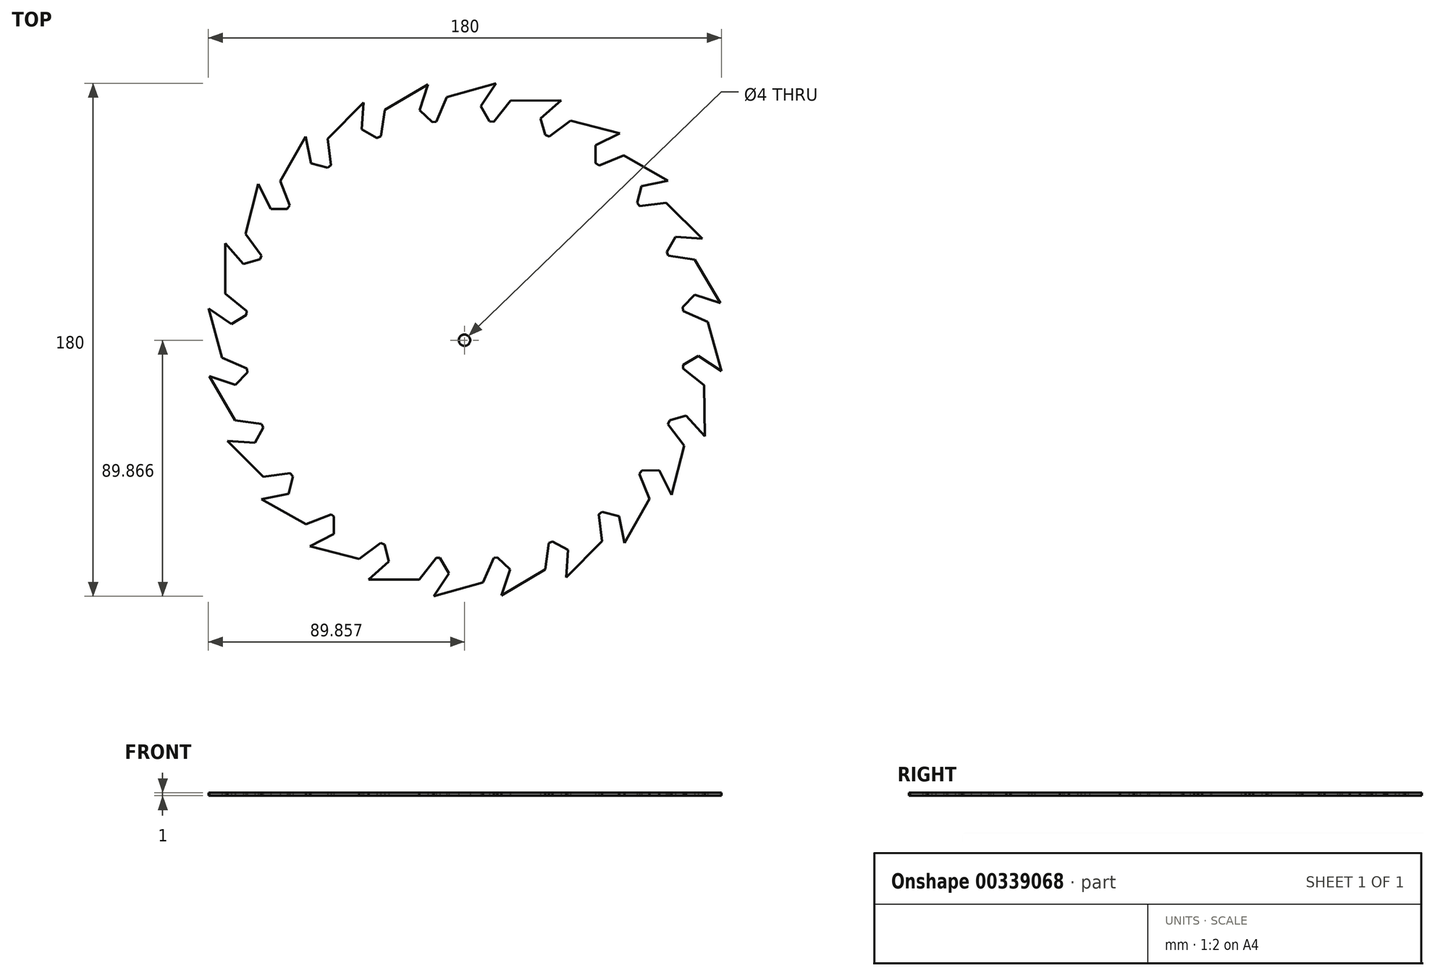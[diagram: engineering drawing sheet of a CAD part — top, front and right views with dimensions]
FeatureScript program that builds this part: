
annotation { "Feature Type Name" : "Feature", "Feature Type Description" : "" }
export const myFeature = defineFeature(function(context is Context, id is Id, definition is map)
    precondition{}
    {
        {
            var Q0;
            Q0=qCreatedBy(makeId("Top.planeOp"),FACE);
            var sketch = newSketch(context, id + "F0", { "sketchPlane" : qUnion([Q0])});
            skLineSegment(sketch, "E0", {"start": v(-178.94, 100.4) * mm, "end": v(-174.2, 83.11) * mm});
            skLineSegment(sketch, "E1", {"start": v(-174.2, 83.11) * mm, "end": v(-165.4, 79.33) * mm});
            skLineSegment(sketch, "E2", {"start": v(-165.4, 79.33) * mm, "end": v(-165.3, 77.88) * mm});
            skLineSegment(sketch, "E3", {"start": v(-165.3, 77.88) * mm, "end": v(-169.49, 73.59) * mm});
            skLineSegment(sketch, "E4", {"start": v(-169.49, 73.59) * mm, "end": v(-178.64, 76.7) * mm});
            skLineSegment(sketch, "E5", {"start": v(-178.64, 76.7) * mm, "end": v(-169.58, 61.17) * mm});
            skLineSegment(sketch, "E6", {"start": v(-169.58, 61.17) * mm, "end": v(-160.31, 59.89) * mm});
            skLineSegment(sketch, "E7", {"start": v(-160.31, 59.89) * mm, "end": v(-159.7, 58.58) * mm});
            skLineSegment(sketch, "E8", {"start": v(-159.7, 58.58) * mm, "end": v(-162.63, 53.3) * mm});
            skLineSegment(sketch, "E9", {"start": v(-162.63, 53.3) * mm, "end": v(-172.27, 53.87) * mm});
            skLineSegment(sketch, "E10", {"start": v(-172.27, 53.87) * mm, "end": v(-159.7, 41.3) * mm});
            skLineSegment(sketch, "E11", {"start": v(-159.7, 41.3) * mm, "end": v(-150.33, 42.55) * mm});
            skLineSegment(sketch, "E12", {"start": v(-150.33, 42.55) * mm, "end": v(-149.3, 41.4) * mm});
            skLineSegment(sketch, "E13", {"start": v(-149.3, 41.4) * mm, "end": v(-150.84, 35.4) * mm});
            skLineSegment(sketch, "E14", {"start": v(-150.84, 35.4) * mm, "end": v(-160.3, 33.5) * mm});
            skLineSegment(sketch, "E15", {"start": v(-160.3, 33.5) * mm, "end": v(-144.68, 24.66) * mm});
            skLineSegment(sketch, "E16", {"start": v(-144.68, 24.66) * mm, "end": v(-135.85, 28.17) * mm});
            skLineSegment(sketch, "E17", {"start": v(-135.85, 28.17) * mm, "end": v(-134.9, 27.37) * mm});
            skLineSegment(sketch, "E18", {"start": v(-134.9, 27.37) * mm, "end": v(-134.9, 21.23) * mm});
            skLineSegment(sketch, "E19", {"start": v(-134.9, 21.23) * mm, "end": v(-143.3, 16.95) * mm});
            skLineSegment(sketch, "E20", {"start": v(-143.3, 16.95) * mm, "end": v(-126.04, 12.48) * mm});
            skLineSegment(sketch, "E21", {"start": v(-126.04, 12.48) * mm, "end": v(-118.52, 18.08) * mm});
            skLineSegment(sketch, "E22", {"start": v(-118.52, 18.08) * mm, "end": v(-117.21, 17.6) * mm});
            skLineSegment(sketch, "E23", {"start": v(-117.21, 17.6) * mm, "end": v(-115.58, 11.63) * mm});
            skLineSegment(sketch, "E24", {"start": v(-115.58, 11.63) * mm, "end": v(-122.7, 5.3) * mm});
            skLineSegment(sketch, "E25", {"start": v(-122.7, 5.3) * mm, "end": v(-104.92, 5.3) * mm});
            skLineSegment(sketch, "E26", {"start": v(-104.92, 5.3) * mm, "end": v(-98.99, 12.84) * mm});
            skLineSegment(sketch, "E27", {"start": v(-98.99, 12.84) * mm, "end": v(-97.75, 12.84) * mm});
            skLineSegment(sketch, "E28", {"start": v(-97.75, 12.84) * mm, "end": v(-94.54, 7.4) * mm});
            skLineSegment(sketch, "E29", {"start": v(-94.54, 7.4) * mm, "end": v(-99.82, -0.6) * mm});
            skLineSegment(sketch, "E30", {"start": v(-99.82, -0.6) * mm, "end": v(-82.64, 4.2) * mm});
            skLineSegment(sketch, "E31", {"start": v(-82.64, 4.2) * mm, "end": v(-78.8, 12.84) * mm});
            skLineSegment(sketch, "E32", {"start": v(-78.8, 12.84) * mm, "end": v(-77.54, 13) * mm});
            skLineSegment(sketch, "E33", {"start": v(-77.54, 13) * mm, "end": v(-73.14, 8.78) * mm});
            skLineSegment(sketch, "E34", {"start": v(-73.14, 8.78) * mm, "end": v(-76.11, -0.27) * mm});
            skLineSegment(sketch, "E35", {"start": v(-76.11, -0.27) * mm, "end": v(-60.77, 8.78) * mm});
            skLineSegment(sketch, "E36", {"start": v(-60.77, 8.78) * mm, "end": v(-59.46, 18.1) * mm});
            skLineSegment(sketch, "E37", {"start": v(-59.46, 18.1) * mm, "end": v(-58.18, 18.66) * mm});
            skLineSegment(sketch, "E38", {"start": v(-58.18, 18.66) * mm, "end": v(-52.76, 15.66) * mm});
            skLineSegment(sketch, "E39", {"start": v(-52.76, 15.66) * mm, "end": v(-53.42, 6.03) * mm});
            skLineSegment(sketch, "E40", {"start": v(-53.42, 6.03) * mm, "end": v(-40.86, 18.77) * mm});
            skLineSegment(sketch, "E41", {"start": v(-40.86, 18.77) * mm, "end": v(-41.97, 28.14) * mm});
            skLineSegment(sketch, "E42", {"start": v(-41.97, 28.14) * mm, "end": v(-40.86, 29.07) * mm});
            skLineSegment(sketch, "E43", {"start": v(-40.86, 29.07) * mm, "end": v(-34.91, 27.53) * mm});
            skLineSegment(sketch, "E44", {"start": v(-34.91, 27.53) * mm, "end": v(-33, 18.1) * mm});
            skLineSegment(sketch, "E45", {"start": v(-33, 18.1) * mm, "end": v(-24.2, 33.57) * mm});
            skLineSegment(sketch, "E46", {"start": v(-24.2, 33.57) * mm, "end": v(-27.71, 42.4) * mm});
            skLineSegment(sketch, "E47", {"start": v(-27.71, 42.4) * mm, "end": v(-26.9, 43.5) * mm});
            skLineSegment(sketch, "E48", {"start": v(-26.9, 43.5) * mm, "end": v(-20.78, 43.6) * mm});
            skLineSegment(sketch, "E49", {"start": v(-20.78, 43.6) * mm, "end": v(-16.44, 35.03) * mm});
            skLineSegment(sketch, "E50", {"start": v(-16.44, 35.03) * mm, "end": v(-12, 52.31) * mm});
            skLineSegment(sketch, "E51", {"start": v(-12, 52.31) * mm, "end": v(-17.67, 59.77) * mm});
            skLineSegment(sketch, "E52", {"start": v(-17.67, 59.77) * mm, "end": v(-17.1, 61.17) * mm});
            skLineSegment(sketch, "E53", {"start": v(-17.1, 61.17) * mm, "end": v(-11.31, 62.78) * mm});
            skLineSegment(sketch, "E54", {"start": v(-11.31, 62.78) * mm, "end": v(-4.8, 55.6) * mm});
            skLineSegment(sketch, "E55", {"start": v(-4.8, 55.6) * mm, "end": v(-4.97, 73.5) * mm});
            skLineSegment(sketch, "E56", {"start": v(-4.97, 73.5) * mm, "end": v(-12.4, 79.3) * mm});
            skLineSegment(sketch, "E57", {"start": v(-12.4, 79.3) * mm, "end": v(-12.32, 80.62) * mm});
            skLineSegment(sketch, "E58", {"start": v(-12.32, 80.62) * mm, "end": v(-7, 83.76) * mm});
            skLineSegment(sketch, "E59", {"start": v(-7, 83.76) * mm, "end": v(1.06, 78.47) * mm});
            skLineSegment(sketch, "E60", {"start": v(1.06, 78.47) * mm, "end": v(-3.74, 95.75) * mm});
            skLineSegment(sketch, "E61", {"start": v(-3.74, 95.75) * mm, "end": v(-12.32, 99.47) * mm});
            skLineSegment(sketch, "E62", {"start": v(-12.32, 99.47) * mm, "end": v(-12.47, 100.94) * mm});
            skLineSegment(sketch, "E63", {"start": v(-12.47, 100.94) * mm, "end": v(-8.35, 105.22) * mm});
            skLineSegment(sketch, "E64", {"start": v(-8.35, 105.22) * mm, "end": v(0.74, 102.23) * mm});
            skLineSegment(sketch, "E65", {"start": v(0.74, 102.23) * mm, "end": v(-8.27, 117.52) * mm});
            skLineSegment(sketch, "E66", {"start": v(-8.27, 117.52) * mm, "end": v(-17.52, 118.92) * mm});
            skLineSegment(sketch, "E67", {"start": v(-17.52, 118.92) * mm, "end": v(-18.1, 120.24) * mm});
            skLineSegment(sketch, "E68", {"start": v(-18.1, 120.24) * mm, "end": v(-15.07, 125.58) * mm});
            skLineSegment(sketch, "E69", {"start": v(-15.07, 125.58) * mm, "end": v(-5.6, 124.93) * mm});
            skLineSegment(sketch, "E70", {"start": v(-5.6, 124.93) * mm, "end": v(-18.3, 137.44) * mm});
            skLineSegment(sketch, "E71", {"start": v(-18.3, 137.44) * mm, "end": v(-27.66, 136.3) * mm});
            skLineSegment(sketch, "E72", {"start": v(-27.66, 136.3) * mm, "end": v(-28.56, 137.44) * mm});
            skLineSegment(sketch, "E73", {"start": v(-28.56, 137.44) * mm, "end": v(-27.03, 143.36) * mm});
            skLineSegment(sketch, "E74", {"start": v(-27.03, 143.36) * mm, "end": v(-17.68, 145.27) * mm});
            skLineSegment(sketch, "E75", {"start": v(-17.68, 145.27) * mm, "end": v(-33.18, 154.08) * mm});
            skLineSegment(sketch, "E76", {"start": v(-33.18, 154.08) * mm, "end": v(-41.85, 150.55) * mm});
            skLineSegment(sketch, "E77", {"start": v(-41.85, 150.55) * mm, "end": v(-43.13, 151.46) * mm});
            skLineSegment(sketch, "E78", {"start": v(-43.13, 151.46) * mm, "end": v(-43.13, 157.6) * mm});
            skLineSegment(sketch, "E79", {"start": v(-43.13, 157.6) * mm, "end": v(-34.62, 161.85) * mm});
            skLineSegment(sketch, "E80", {"start": v(-34.62, 161.85) * mm, "end": v(-51.87, 166.3) * mm});
            skLineSegment(sketch, "E81", {"start": v(-51.87, 166.3) * mm, "end": v(-59.38, 160.69) * mm});
            skLineSegment(sketch, "E82", {"start": v(-59.38, 160.69) * mm, "end": v(-60.77, 161.31) * mm});
            skLineSegment(sketch, "E83", {"start": v(-60.77, 161.31) * mm, "end": v(-62.39, 167.12) * mm});
            skLineSegment(sketch, "E84", {"start": v(-62.39, 167.12) * mm, "end": v(-55.17, 173.48) * mm});
            skLineSegment(sketch, "E85", {"start": v(-55.17, 173.48) * mm, "end": v(-72.98, 173.31) * mm});
            skLineSegment(sketch, "E86", {"start": v(-72.98, 173.31) * mm, "end": v(-78.78, 165.94) * mm});
            skLineSegment(sketch, "E87", {"start": v(-78.78, 165.94) * mm, "end": v(-80.32, 166.05) * mm});
            skLineSegment(sketch, "E88", {"start": v(-80.32, 166.05) * mm, "end": v(-83.43, 171.32) * mm});
            skLineSegment(sketch, "E89", {"start": v(-83.43, 171.32) * mm, "end": v(-77.97, 179.4) * mm});
            skLineSegment(sketch, "E90", {"start": v(-77.97, 179.4) * mm, "end": v(-95.37, 174.56) * mm});
            skLineSegment(sketch, "E91", {"start": v(-95.37, 174.56) * mm, "end": v(-98.99, 165.9) * mm});
            skLineSegment(sketch, "E92", {"start": v(-98.99, 165.9) * mm, "end": v(-100.43, 165.76) * mm});
            skLineSegment(sketch, "E93", {"start": v(-100.43, 165.76) * mm, "end": v(-104.83, 169.98) * mm});
            skLineSegment(sketch, "E94", {"start": v(-104.83, 169.98) * mm, "end": v(-101.85, 179.02) * mm});
            skLineSegment(sketch, "E95", {"start": v(-101.85, 179.02) * mm, "end": v(-117.04, 170.07) * mm});
            skLineSegment(sketch, "E96", {"start": v(-117.04, 170.07) * mm, "end": v(-118.39, 160.87) * mm});
            skLineSegment(sketch, "E97", {"start": v(-118.39, 160.87) * mm, "end": v(-119.78, 160.18) * mm});
            skLineSegment(sketch, "E98", {"start": v(-119.78, 160.18) * mm, "end": v(-125.14, 163.23) * mm});
            skLineSegment(sketch, "E99", {"start": v(-125.14, 163.23) * mm, "end": v(-124.49, 172.71) * mm});
            skLineSegment(sketch, "E100", {"start": v(-124.49, 172.71) * mm, "end": v(-137.05, 159.97) * mm});
            skLineSegment(sketch, "E101", {"start": v(-137.05, 159.97) * mm, "end": v(-135.89, 150.7) * mm});
            skLineSegment(sketch, "E102", {"start": v(-135.89, 150.7) * mm, "end": v(-137.05, 149.78) * mm});
            skLineSegment(sketch, "E103", {"start": v(-137.05, 149.78) * mm, "end": v(-142.98, 151.3) * mm});
            skLineSegment(sketch, "E104", {"start": v(-142.98, 151.3) * mm, "end": v(-144.89, 160.7) * mm});
            skLineSegment(sketch, "E105", {"start": v(-144.89, 160.7) * mm, "end": v(-153.75, 145.1) * mm});
            skLineSegment(sketch, "E106", {"start": v(-153.75, 145.1) * mm, "end": v(-150.39, 136.64) * mm});
            skLineSegment(sketch, "E107", {"start": v(-150.39, 136.64) * mm, "end": v(-151.35, 135.3) * mm});
            skLineSegment(sketch, "E108", {"start": v(-151.35, 135.3) * mm, "end": v(-157.08, 135.3) * mm});
            skLineSegment(sketch, "E109", {"start": v(-157.08, 135.3) * mm, "end": v(-161.46, 144.07) * mm});
            skLineSegment(sketch, "E110", {"start": v(-161.46, 144.07) * mm, "end": v(-165.97, 126.52) * mm});
            skLineSegment(sketch, "E111", {"start": v(-165.97, 126.52) * mm, "end": v(-160.27, 118.92) * mm});
            skLineSegment(sketch, "E112", {"start": v(-160.27, 118.92) * mm, "end": v(-160.78, 117.62) * mm});
            skLineSegment(sketch, "E113", {"start": v(-160.78, 117.62) * mm, "end": v(-166.66, 115.99) * mm});
            skLineSegment(sketch, "E114", {"start": v(-166.66, 115.99) * mm, "end": v(-173.07, 123.26) * mm});
            skLineSegment(sketch, "E115", {"start": v(-173.07, 123.26) * mm, "end": v(-173.07, 105.62) * mm});
            skLineSegment(sketch, "E116", {"start": v(-173.07, 105.62) * mm, "end": v(-165.53, 99.51) * mm});
            skLineSegment(sketch, "E117", {"start": v(-165.53, 99.51) * mm, "end": v(-165.64, 98.05) * mm});
            skLineSegment(sketch, "E118", {"start": v(-165.64, 98.05) * mm, "end": v(-170.93, 94.93) * mm});
            skLineSegment(sketch, "E119", {"start": v(-170.93, 94.93) * mm, "end": v(-178.94, 100.4) * mm});
            skCircle(sketch, "E120", {"center": v(-89.08, 89.27) * mm, "radius": 2 * mm});
            skSolve(sketch);
        }
        {
            var Q0;
            Q0=makeQuery(id+"F0.imprint","IMPRINT",FACE,{"disambiguationData":[TD([[makeQuery(id+"F0.imprint","IMPRINT",EDGE,{"derivedFrom":sQuery(id+"F0.wireOp",EDGE,"E0")}),1.0]])]});
            extrude(context, id + "F1", {"entities" : qUnion([Q0]), "depth" : 1 * mm, "offsetDistance" : 25 * mm});
        }
    });
